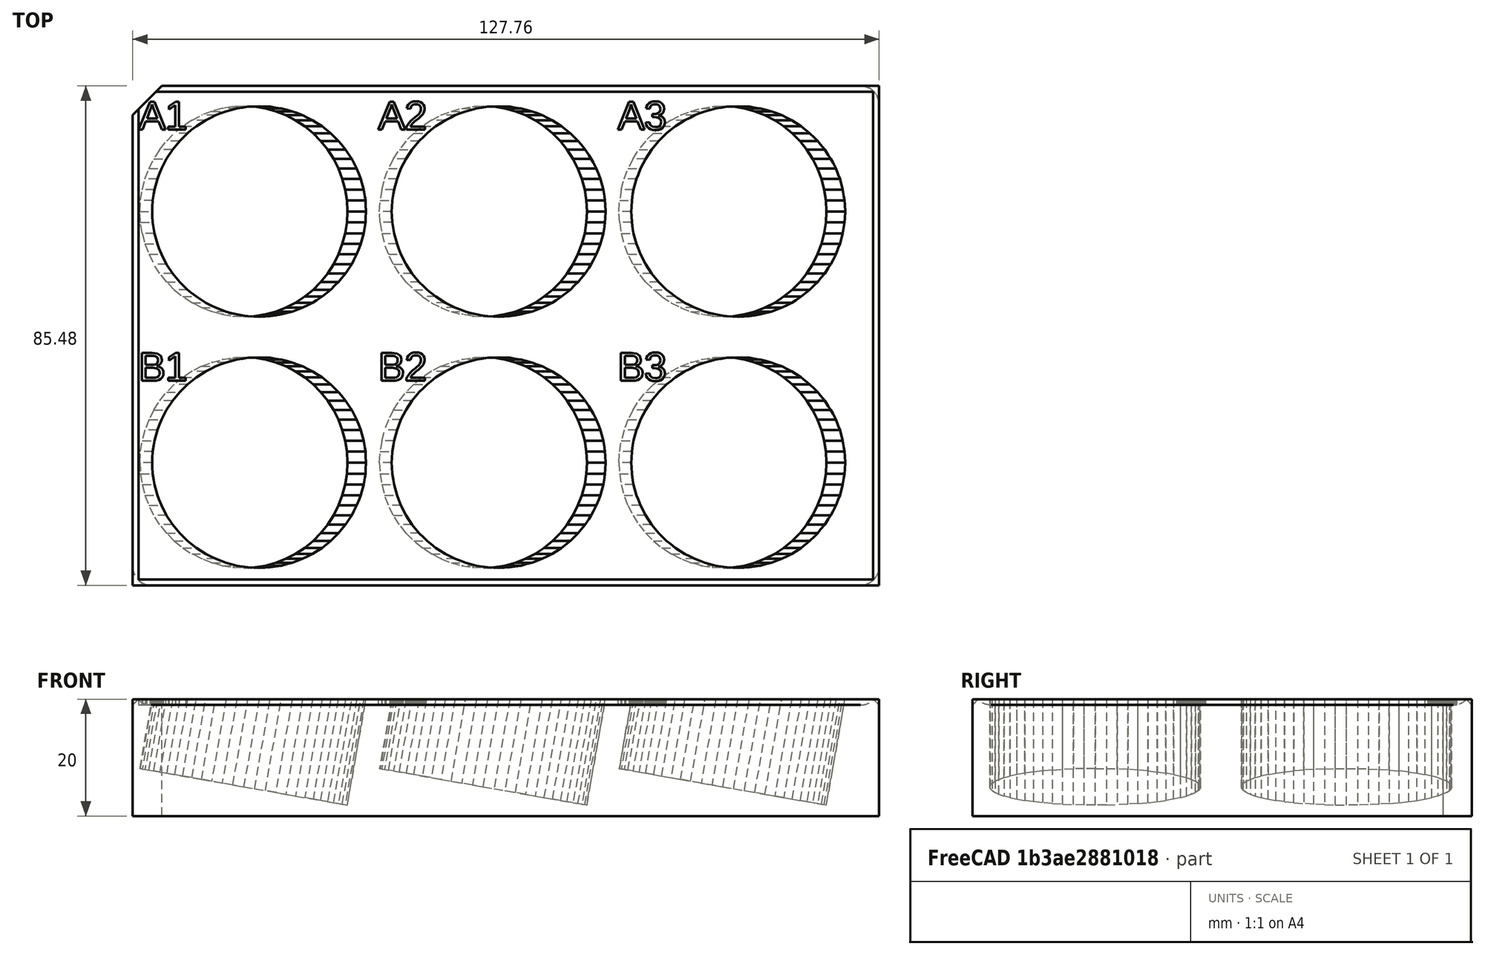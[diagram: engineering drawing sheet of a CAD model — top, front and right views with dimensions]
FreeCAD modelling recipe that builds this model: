
FCSTD DOCUMENT  (FreeCAD 0.18.4R)
Label: rack_with_filets
License: All rights reserved
LicenseURL: http://en.wikipedia.org/wiki/All_rights_reserved
objects: Part::Feature×2, Part::Fillet×2, Mesh::Feature×1, Part::Chamfer×1
note: 5 computed .brp shape members not serialized (recipe doc carries the construction recipe); baked Part::Feature solids carry a one-line shape summary decoded from their .brp

FEATURE [Mesh::Feature] rack_for_urine_vials
FEATURE [Part::Feature] rack_for_urine_vials001
  shape: bbox 127.8 x 85.48 x 20 mm, 4032 faces, 0 solids (baked)
FEATURE [Part::Feature] rack_for_urine_vials001001  label="rack_for_urine_vials002"
  shape: bbox 127.8 x 85.48 x 20 mm, 1866 faces, 0 solids (baked)
FEATURE [Part::Chamfer] Chamfer
  Base = -> rack_for_urine_vials001001
  Edges = 4 edges r=1: [Edge592,Edge593,Edge594,Edge596]
FEATURE [Part::Fillet] Fillet
  Base = -> Chamfer
  Edges = 2 edges r=3.18: [Edge2819,Edge2820]
FEATURE [Part::Fillet] Fillet001
  Base = -> Fillet
  Edges = 1 edges r=3.18: [Edge1055]
